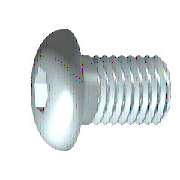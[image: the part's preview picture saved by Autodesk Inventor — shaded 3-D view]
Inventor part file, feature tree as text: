
AUTODESK INVENTOR PART (.ipt)
format: ipt  version: 2022 (Build 260153000, 153)  size: 200,704 bytes
history: native  units: mm (DEFAULTED — no unit token found)
features: sketch x2, extrude x1, plane x1, fillet x1
ambient origin geometry x7: Origin, YZ Plane, XY Plane, X Axis, Y Axis, Z Axis, Center Point
bodies: Solid1 (feature_tree), Body (feature_tree)
feature tree (5):
  extrude  "Slot"  Depth=2.2mm
  plane  "Work Plane1"
  fillet  "Fillet2"  Radius=2.2mm
  sketch  "Sketch1"  dims[d1=9.9mm d2=0.429515mm d3=2.2mm]
  sketch  "Sketch2"  dims[d4=1.3mm d5=60.0deg d6=4.0mm d7=4.0mm d8=2.886751mm d9=7.6mm d10=90.0deg d11=10.0mm d12=0.0mm d13=9.9mm d14=0.0mm d15=0.429415mm d16=0.429415mm d17=1.9mm d19=0.0mm d26=12.0mm d27=45.0deg d28=0.0mm d29=0.0mm d30=0.4mm]
